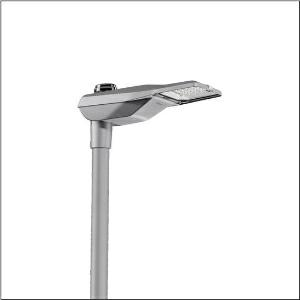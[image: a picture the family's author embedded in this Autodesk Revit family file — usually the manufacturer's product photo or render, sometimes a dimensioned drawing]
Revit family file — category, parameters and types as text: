
# Revit family: streetlight_sl_21_micro___stw1_0a_5xe5e37n08db_8c5c
name_source: partatom
category: Lighting Fixtures
units: mm (PartAtom-declared; Revit-internal decimal feet)

## family parameters
Cut with Voids When Loaded = No
Host = Face
Light Source = No
Part Type = Normal
Room Calculation Point = No
Round Connector Dimension = Use Diameter
Shared = No

## types (1)
- --- (1 x LED, 5110 lm, 39.1 W, 3000K)
    Apparent Load = 39 VA
    CIE Flux Codes = 38 75 98 100 100
    Color Rendering = 70
    Color Temperature = 3000K
    Default Elevation = 1800 mm
    Description = Streetlight SL 21 micro, mast luminaire, primary light control with lens, of PMMA, primary optical cover: cover, of toughened safety glass, transparent, light distribution: STW1.0a, light emission: direct distribution, primary light characteristic: asymmetric, installation type: post-top, LED, 3G 1.5mm², High Power LED, rated luminous flux: 5.110lm, luminous efficacy: 131lm/W, light colour: 730, colour temperature: 3000K, control: overheat protection, presetting dimming linear, constant luminous flux control, time-dependent luminous flux control, flexible luminous flux parameterisation, mains connection: 230..240V, AC, 50/60Hz, connection cable pre-assembled, cable length: 6,5m, wiring characteristics: H07RN-F, start of lifetime: 39W, end of service life: 41W, reduction: 18W, luminaire housing, of diecast aluminium (EN AC-44300), powder-coated, Siteco® metallic grey (DB 702S), corrosivity category C5 mid according to DIN EN ISO 12944, multi-level sealing system, sealing non-destructively replaceable, inclination adjustable: 0°, 5°, 10°, 15°, length: 528mm, width: 235mm, height: 110mm, spigot size: 76/60mm (post-top), protection rating (complete): IP66, insulation class (complete): insulation class I (protective earthing), certification: CE, ENEC, ENEC+, VDE, impact resistance: IK09, permissible operating ambient temperature for outdoor applications: -40..+50°C, standard-compliant lighting for roads and squares, packaging unit: 1 piece

Light Distribution: STW1.0a
    Height = 110 mm
    Lamp = 1 x LED
    Lamp Light Flux = 5110 lm
    Lamp Power = 39.1 W
    Lamp count = 1
    Length = 528 mm
    Luminous efficacy = 131 lm/W
    Manufacturer = Siteco
    ModVariant = No
    Model = 5XE5E37N08DB
    Number of Poles = 1
    OnlyDefault = Yes
    Power Factor = 1
    Product Name = Streetlight SL 21 micro | STW1.0a
    Product group = mast luminaire | pylon top
    ProductGroupID = 6100
    Protection Class = Protection class I
    Protection Degree = IP 66
    RLX_Detail_Level = 1
    RLX_Emergency_Light_Flux = 0 lm
    RLX_Emergency_Type = 0
    RLX_Emergency_Type_DB = No
    RlxData = <blob elided: 99401 chars, md5=98c542fa>
    Socket = socket
    Standby Power = 0 W
    System Light Flux = 5110 lm
    System Power = 39 W
    Type Comments = factory setting: luminous flux: 100 % | dim-lin: 254 | 765 mA
    Type Image = l_1294375.jpg
    URL = http://relux.com
    VarID = @adj_085201
    Voltage = 0 V
    Weight = 0.00 kg
    Width = 235 mm

## geometry (parser evidence)
native form markers: Blend x4, Sweep x10
no freeform markers — native parametric forms only
